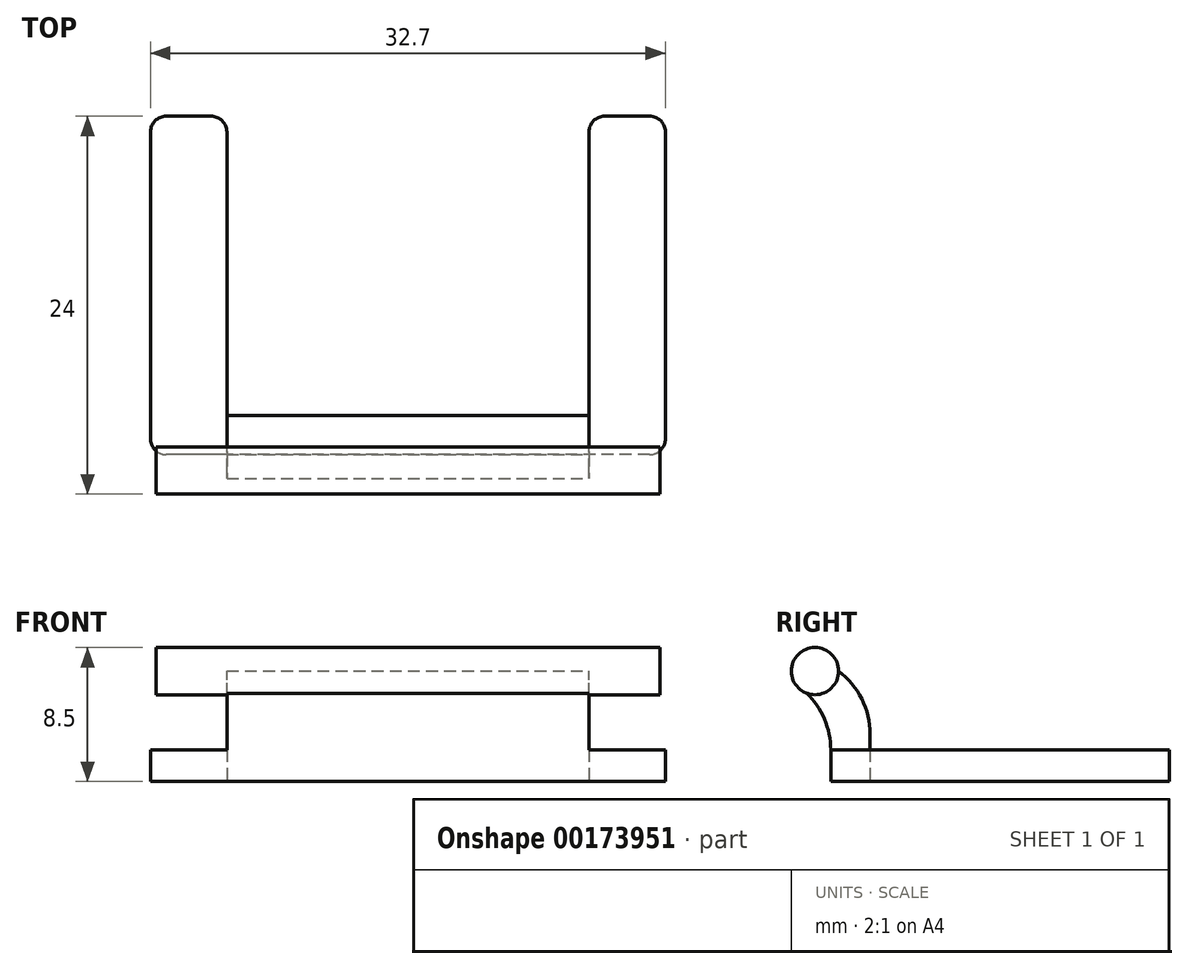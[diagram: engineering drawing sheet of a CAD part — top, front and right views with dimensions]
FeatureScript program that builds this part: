
annotation { "Feature Type Name" : "Feature", "Feature Type Description" : "" }
export const myFeature = defineFeature(function(context is Context, id is Id, definition is map)
    precondition{}
    {
        {
            var Q0;
            Q0=qCreatedBy(makeId("Top.planeOp"),FACE);
            var sketch = newSketch(context, id + "F0", { "sketchPlane" : qUnion([Q0])});
            skLineSegment(sketch, "E0.bottom", {"start": v(15.35, -10.75) * mm, "end": v(-15.35, -10.75) * mm});
            skLineSegment(sketch, "E0.left", {"start": v(16.35, -9.75) * mm, "end": v(16.35, 9.75) * mm});
            skLineSegment(sketch, "E0.right", {"start": v(-16.35, -9.75) * mm, "end": v(-16.35, 9.75) * mm});
            skPoint(sketch, "E0.middle", {"position": v(0, 0) * mm});
            skLineSegment(sketch, "E1.top", {"start": v(-11.5, -8.25) * mm, "end": v(11.5, -8.25) * mm});
            skLineSegment(sketch, "E1.left", {"start": v(-11.5, 9.75) * mm, "end": v(-11.5, -8.25) * mm});
            skLineSegment(sketch, "E1.right", {"start": v(11.5, 9.75) * mm, "end": v(11.5, -8.25) * mm});
            skLineSegment(sketch, "E2", {"start": v(-15.35, 10.75) * mm, "end": v(-12.5, 10.75) * mm});
            skLineSegment(sketch, "E3", {"start": v(12.5, 10.75) * mm, "end": v(15.35, 10.75) * mm});
            skPoint(sketch, "E4.visualSharp", {"position": v(-16.35, 10.75) * mm});
            skArc(sketch, "E4.filletArc", {"start": v(-15.35, 10.75) * mm, "mid": v(-16.06, 10.46) * mm, "end": v(-16.35, 9.75) * mm});
            skPoint(sketch, "E5.visualSharp", {"position": v(-11.5, 10.75) * mm});
            skArc(sketch, "E5.filletArc", {"start": v(-11.5, 9.75) * mm, "mid": v(-11.8, 10.46) * mm, "end": v(-12.5, 10.75) * mm});
            skPoint(sketch, "E6.visualSharp", {"position": v(-16.35, -10.75) * mm});
            skArc(sketch, "E6.filletArc", {"start": v(-16.35, -9.75) * mm, "mid": v(-16.06, -10.46) * mm, "end": v(-15.35, -10.75) * mm});
            skPoint(sketch, "E7.visualSharp", {"position": v(16.35, -10.75) * mm});
            skArc(sketch, "E7.filletArc", {"start": v(15.35, -10.75) * mm, "mid": v(16.06, -10.46) * mm, "end": v(16.35, -9.75) * mm});
            skPoint(sketch, "E8.visualSharp", {"position": v(16.35, 10.75) * mm});
            skArc(sketch, "E8.filletArc", {"start": v(16.35, 9.75) * mm, "mid": v(16.06, 10.46) * mm, "end": v(15.35, 10.75) * mm});
            skPoint(sketch, "E9.visualSharp", {"position": v(11.5, 10.75) * mm});
            skArc(sketch, "E9.filletArc", {"start": v(12.5, 10.75) * mm, "mid": v(11.8, 10.46) * mm, "end": v(11.5, 9.75) * mm});
            skSolve(sketch);
        }
        {
            var Q0;
            Q0 = qSketchRegion(id + "F0", true);
            extrude(context, id + "F1", {"entities" : qUnion([Q0]), "depth" : 2 * mm});
        }
        {
            var Q0;
            Q0=makeQuery(id+"F1.opExtrude","CAP_FACE",FACE,{"disambiguationData":[OSD([sQuery(id+"F0.wireOp",EDGE,"E0.bottom"),sQuery(id+"F0.wireOp",EDGE,"E0.left"),sQuery(id+"F0.wireOp",EDGE,"E0.right"),sQuery(id+"F0.wireOp",EDGE,"E1.top"),sQuery(id+"F0.wireOp",EDGE,"E1.left"),sQuery(id+"F0.wireOp",EDGE,"E1.right"),sQuery(id+"F0.wireOp",EDGE,"E2"),sQuery(id+"F0.wireOp",EDGE,"E3")])],"isStart":false});
            var sketch = newSketch(context, id + "F2", { "sketchPlane" : qUnion([Q0])});
            skLineSegment(sketch, "E10.bottom", {"start": v(-11.5, -8.25) * mm, "end": v(11.5, -8.25) * mm});
            skLineSegment(sketch, "E10.top", {"start": v(-11.5, -10.75) * mm, "end": v(11.5, -10.75) * mm});
            skLineSegment(sketch, "E10.left", {"start": v(-11.5, -8.25) * mm, "end": v(-11.5, -10.75) * mm});
            skLineSegment(sketch, "E10.right", {"start": v(11.5, -8.25) * mm, "end": v(11.5, -10.75) * mm});
            skSolve(sketch);
        }
        {
            var Q0;
            Q0 = qSketchRegion(id + "F2", true);
            extrude(context, id + "F3", {"entities" : qUnion([Q0]), "operationType" : NewBodyOperationType.ADD, "depth" : 5 * mm});
        }
        {
            var Q0;
            Q0=makeQuery(id+"F3.opExtrude","SWEPT_FACE",FACE,{"disambiguationData":[OSD([sQuery(id+"F2.wireOp",EDGE,"E10.right")])]});
            cPlane(context, id + "F4", {"entities" : qUnion([Q0]), "cplaneType" : CPlaneType.OFFSET, "offset" : 4.5 * mm, "width" : 150 * mm, "height" : 150 * mm});
        }
        {
            var Q0;
            Q0=makeQuery(id+"F3.opExtrude","SWEPT_FACE",FACE,{"disambiguationData":[OSD([sQuery(id+"F2.wireOp",EDGE,"E10.left")])]});
            cPlane(context, id + "F5", {"entities" : qUnion([Q0]), "cplaneType" : CPlaneType.OFFSET, "offset" : 4.5 * mm, "width" : 150 * mm, "height" : 150 * mm});
        }
        {
            var Q0;
            Q0=qCreatedBy(id+"F4.planeOp",FACE);
            var sketch = newSketch(context, id + "F6", { "sketchPlane" : qUnion([Q0])});
            skCircle(sketch, "E11", {"center": v(-11.75, 7) * mm, "radius": 1.5 * mm});
            skSolve(sketch);
        }
        {
            var Q0;
            Q0 = qSketchRegion(id + "F6", true);
            var Q1;
            Q1=qCreatedBy(id+"F5.planeOp",FACE);
            extrude(context, id + "F7", {"entities" : qUnion([Q0]), "operationType" : NewBodyOperationType.ADD, "endBound" : BoundingType.UP_TO_SURFACE, "oppositeDirection" : true, "endBoundEntityFace" : qUnion([Q1]), "depth" : 25 * mm});
        }
        {
            var Q0;
            Q0=makeQuery(id+"F3.opExtrude","SWEPT_FACE",FACE,{"disambiguationData":[OSD([sQuery(id+"F2.wireOp",EDGE,"E10.right")])]});
            var sketch = newSketch(context, id + "F8", { "sketchPlane" : qUnion([Q0])});
            skLineSegment(sketch, "E12", {"start": v(-13, 6.18) * mm, "end": v(-10.75, 6.18) * mm});
            skLineSegment(sketch, "E13", {"start": v(-10.75, 6.18) * mm, "end": v(-10.75, 2) * mm});
            skCircle(sketch, "E14.0", {"center": v(-11.75, 7) * mm, "radius": 1.5 * mm});
            skPoint(sketch, "E15.orphan", {"position": v(-13, 6.18) * mm});
            skArc(sketch, "E16", {"start": v(-10.75, 2) * mm, "mid": v(-11.35, 4.37) * mm, "end": v(-13, 6.18) * mm});
            skSolve(sketch);
        }
        {
            var Q0;
            Q0 = qSketchRegion(id + "F8", true);
            var Q1;
            Q1=makeQuery(id+"F3.opExtrude","SWEPT_FACE",FACE,{"disambiguationData":[OSD([sQuery(id+"F2.wireOp",EDGE,"E10.left")])]});
            extrude(context, id + "F9", {"entities" : qUnion([Q0]), "operationType" : NewBodyOperationType.ADD, "endBound" : BoundingType.UP_TO_SURFACE, "oppositeDirection" : true, "endBoundEntityFace" : qUnion([Q1]), "depth" : 25 * mm});
        }
        {
            var Q0;
            Q0=makeQuery(id+"F3.opExtrude","CAP_EDGE",EDGE,{"disambiguationData":[OSD([sQuery(id+"F2.wireOp",EDGE,"E10.bottom")])],"isStart":false});
            fillet(context, id + "F10", {"entities" : qUnion([Q0]), "radius" : 5 * mm, "tangentPropagation" : true, "allowEdgeOverflow" : false});
        }
    });
